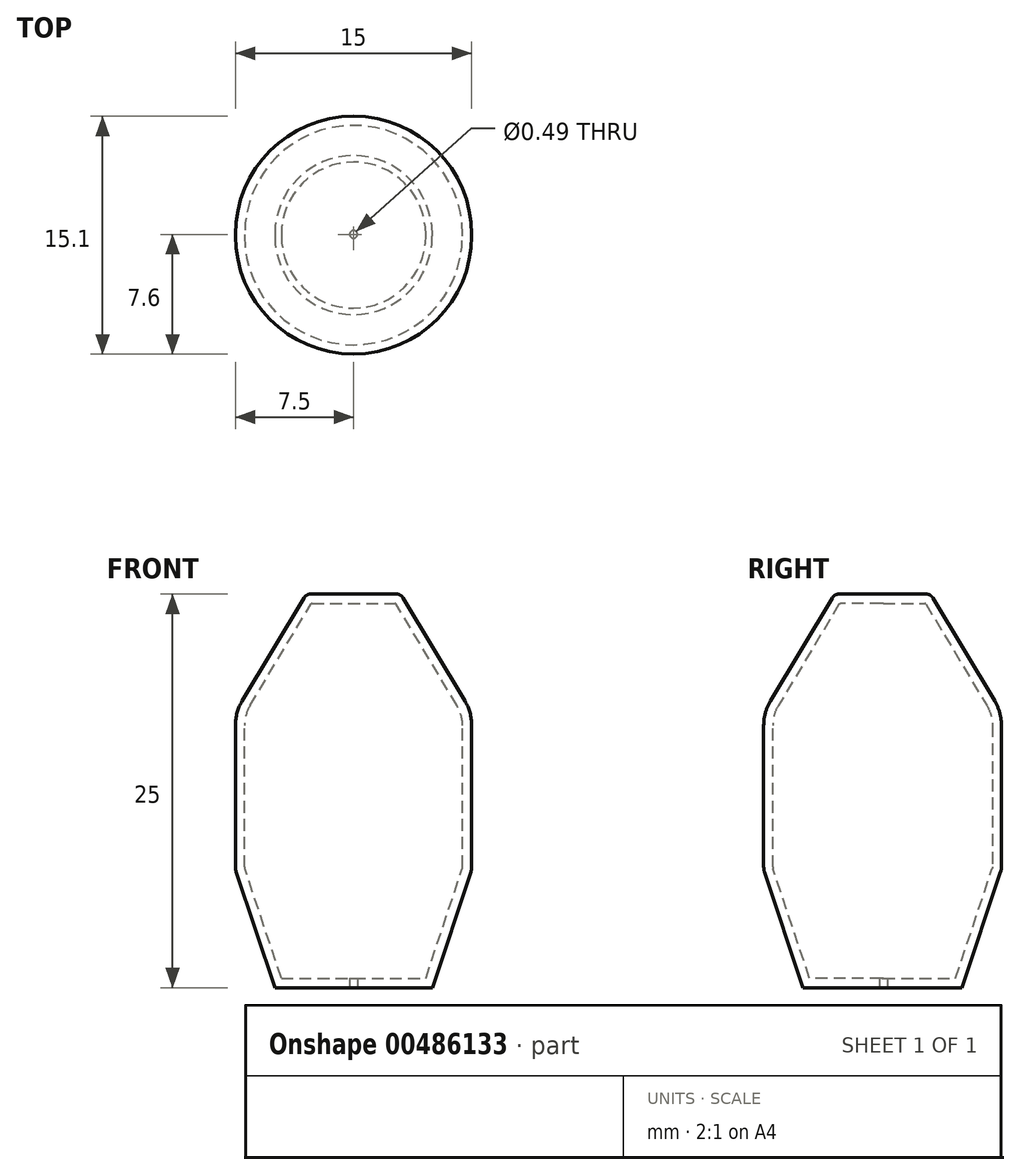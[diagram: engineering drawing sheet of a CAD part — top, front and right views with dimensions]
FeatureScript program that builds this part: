
annotation { "Feature Type Name" : "Feature", "Feature Type Description" : "" }
export const myFeature = defineFeature(function(context is Context, id is Id, definition is map)
    precondition{}
    {
        {
            assignVariable(context, id + "F0", {"name" : "l2", "anyValue" : 0.1});
        }
        {
            var Q0;
            Q0=qCreatedBy(makeId("Front.planeOp"),FACE);
            var sketch = newSketch(context, id + "F1", { "sketchPlane" : qUnion([Q0])});
            skLineSegment(sketch, "E0", {"start": v(0, 0) * mm, "end": v(5, 0) * mm});
            skLineSegment(sketch, "E1", {"start": v(7.5, 7.66) * mm, "end": v(7.5, 16.67) * mm});
            skLineSegment(sketch, "E2", {"start": v(2.72, 25) * mm, "end": v(0, 25) * mm});
            skLineSegment(sketch, "E3", {"start": v(5, 0) * mm, "end": v(7.45, 7.35) * mm});
            skLineSegment(sketch, "E4", {"start": v(7.07, 18.21) * mm, "end": v(3.15, 24.76) * mm});
            skLineSegment(sketch, "E5", {"start": v(0, 0) * mm, "end": v(0, 0.6) * mm});
            skLineSegment(sketch, "E6", {"start": v(0, 0.6) * mm, "end": v(4.59, 0.6) * mm});
            skLineSegment(sketch, "E7", {"start": v(6.92, 7.66) * mm, "end": v(6.92, 16.67) * mm});
            skLineSegment(sketch, "E8", {"start": v(6.58, 17.91) * mm, "end": v(2.7, 24.36) * mm});
            skLineSegment(sketch, "E9", {"start": v(2.64, 24.4) * mm, "end": v(0, 24.4) * mm});
            skLineSegment(sketch, "E10", {"start": v(0, 24.4) * mm, "end": v(0, 25) * mm});
            skLineSegment(sketch, "E11", {"start": v(4.59, 0.6) * mm, "end": v(6.9, 7.53) * mm});
            skPoint(sketch, "E12.visualSharp", {"position": v(7.5, 7.5) * mm});
            skArc(sketch, "E12.filletArc", {"start": v(7.45, 7.35) * mm, "mid": v(7.49, 7.5) * mm, "end": v(7.5, 7.66) * mm});
            skPoint(sketch, "E13.visualSharp", {"position": v(7.5, 17.5) * mm});
            skArc(sketch, "E13.filletArc", {"start": v(7.5, 16.67) * mm, "mid": v(7.4, 17.47) * mm, "end": v(7.07, 18.21) * mm});
            skPoint(sketch, "E14.visualSharp", {"position": v(3, 25) * mm});
            skArc(sketch, "E14.filletArc", {"start": v(3.15, 24.76) * mm, "mid": v(2.96, 24.94) * mm, "end": v(2.72, 25) * mm});
            skPoint(sketch, "E15.visualSharp", {"position": v(2.68, 24.4) * mm});
            skArc(sketch, "E15.filletArc", {"start": v(2.7, 24.36) * mm, "mid": v(2.68, 24.39) * mm, "end": v(2.64, 24.4) * mm});
            skPoint(sketch, "E16.visualSharp", {"position": v(6.92, 17.34) * mm});
            skArc(sketch, "E16.filletArc", {"start": v(6.92, 16.67) * mm, "mid": v(6.83, 17.32) * mm, "end": v(6.58, 17.91) * mm});
            skPoint(sketch, "E17.visualSharp", {"position": v(6.92, 7.6) * mm});
            skArc(sketch, "E17.filletArc", {"start": v(6.9, 7.53) * mm, "mid": v(6.91, 7.6) * mm, "end": v(6.92, 7.66) * mm});
            skSolve(sketch);
        }
        {
            var Q0;
            Q0=makeQuery(id+"F1.imprint","IMPRINT",FACE,{"disambiguationData":[TD([[makeQuery(id+"F1.imprint","IMPRINT",EDGE,{"derivedFrom":sQuery(id+"F1.wireOp",EDGE,"E0")}),1.0]])]});
            extrude(context, id + "F2", {"entities" : qUnion([Q0]), "depth" : (getVariable(context, 'l2')) * mm});
        }
        {
            var Q0;
            Q0=makeQuery(id+"F2.opExtrude","CAP_FACE",FACE,{"disambiguationData":[OSD([sQuery(id+"F1.wireOp",EDGE,"E0"),sQuery(id+"F1.wireOp",EDGE,"E1"),sQuery(id+"F1.wireOp",EDGE,"E2"),sQuery(id+"F1.wireOp",EDGE,"E3"),sQuery(id+"F1.wireOp",EDGE,"E4"),sQuery(id+"F1.wireOp",EDGE,"E5"),sQuery(id+"F1.wireOp",EDGE,"E6"),sQuery(id+"F1.wireOp",EDGE,"E7"),sQuery(id+"F1.wireOp",EDGE,"E8"),sQuery(id+"F1.wireOp",EDGE,"E9"),sQuery(id+"F1.wireOp",EDGE,"E10"),sQuery(id+"F1.wireOp",EDGE,"E11"),sQuery(id+"F1.wireOp",EDGE,"E12.filletArc"),sQuery(id+"F1.wireOp",EDGE,"E13.filletArc"),sQuery(id+"F1.wireOp",EDGE,"E14.filletArc"),sQuery(id+"F1.wireOp",EDGE,"E15.filletArc"),sQuery(id+"F1.wireOp",EDGE,"E16.filletArc"),sQuery(id+"F1.wireOp",EDGE,"E17.filletArc")])],"isStart":false});
            var Q1;
            Q1=makeQuery(id+"F2.opExtrude","CAP_EDGE",EDGE,{"disambiguationData":[OSD([sQuery(id+"F1.wireOp",EDGE,"E10")])],"isStart":false});
            revolve(context, id + "F3", {"operationType" : NewBodyOperationType.ADD, "entities" : qUnion([Q0]), "axis" : qUnion([Q1]), "revolveType" : RevolveType.ONE_DIRECTION, "oppositeDirection" : true, "angle" : 180 * degree});
        }
        {
            var Q0;
            Q0=makeQuery(id+"F1.imprint","IMPRINT",FACE,{"disambiguationData":[TD([[makeQuery(id+"F1.imprint","IMPRINT",EDGE,{"derivedFrom":sQuery(id+"F1.wireOp",EDGE,"E0")}),1.0]])]});
            var Q1;
            Q1=sQuery(id+"F1.wireOp",EDGE,"E10");
            revolve(context, id + "F4", {"operationType" : NewBodyOperationType.ADD, "entities" : qUnion([Q0]), "axis" : qUnion([Q1]), "revolveType" : RevolveType.ONE_DIRECTION, "angle" : 180 * degree});
        }
        {
            var Q0;
            Q0=makeQuery(id+"F3.opRevolve","CAP_FACE",FACE,{"disambiguationData":[OSD([sQuery(id+"F1.wireOp",EDGE,"E0"),sQuery(id+"F1.wireOp",EDGE,"E1"),sQuery(id+"F1.wireOp",EDGE,"E2"),sQuery(id+"F1.wireOp",EDGE,"E3"),sQuery(id+"F1.wireOp",EDGE,"E4"),sQuery(id+"F1.wireOp",EDGE,"E5"),sQuery(id+"F1.wireOp",EDGE,"E6"),sQuery(id+"F1.wireOp",EDGE,"E7"),sQuery(id+"F1.wireOp",EDGE,"E8"),sQuery(id+"F1.wireOp",EDGE,"E9"),sQuery(id+"F1.wireOp",EDGE,"E10"),sQuery(id+"F1.wireOp",EDGE,"E11"),sQuery(id+"F1.wireOp",EDGE,"E12.filletArc"),sQuery(id+"F1.wireOp",EDGE,"E13.filletArc"),sQuery(id+"F1.wireOp",EDGE,"E14.filletArc"),sQuery(id+"F1.wireOp",EDGE,"E15.filletArc"),sQuery(id+"F1.wireOp",EDGE,"E16.filletArc"),sQuery(id+"F1.wireOp",EDGE,"E17.filletArc")])],"isStart":true});
            extrude(context, id + "F5", {"entities" : qUnion([Q0]), "operationType" : NewBodyOperationType.ADD, "depth" : (getVariable(context, 'l2')) * mm});
        }
        {
            var Q0;
            {var subQ0=sQuery(id+"F1.wireOp",EDGE,"E0");Q0=makeQuery(id+"F5.boolean.opBoolean","MERGE",FACE,{"derivedFrom":[makeQuery(id+"F4.boolean.opBoolean","MERGE",FACE,{"derivedFrom":[makeQuery(id+"F3.boolean.opBoolean","MERGE",FACE,{"derivedFrom":[makeQuery(id+"F2.opExtrude","SWEPT_FACE",FACE,{"disambiguationData":[OSD([subQ0])]}),makeQuery(id+"F3.opRevolve","SWEPT_FACE",FACE,{"disambiguationData":[OSD([subQ0])]})]}),makeQuery(id+"F4.opRevolve","SWEPT_FACE",FACE,{"disambiguationData":[OSD([subQ0])]})]}),makeQuery(id+"F5.opExtrude","SWEPT_FACE",FACE,{"disambiguationData":[OSD([subQ0])]})]});}
            var sketch = newSketch(context, id + "F6", { "sketchPlane" : qUnion([Q0])});
            skCircle(sketch, "E18", {"center": v(0, 0) * mm, "radius": 0.24 * mm});
            skSolve(sketch);
        }
        {
            var Q0;
            Q0=makeQuery(id+"F6.imprint","IMPRINT",FACE,{"disambiguationData":[TD([[makeQuery(id+"F6.imprint","IMPRINT",EDGE,{"derivedFrom":sQuery(id+"F6.wireOp",EDGE,"E18")}),1.0]])]});
            extrude(context, id + "F7", {"entities" : qUnion([Q0]), "operationType" : NewBodyOperationType.REMOVE, "oppositeDirection" : true, "depth" : 1 * mm});
        }
    });
